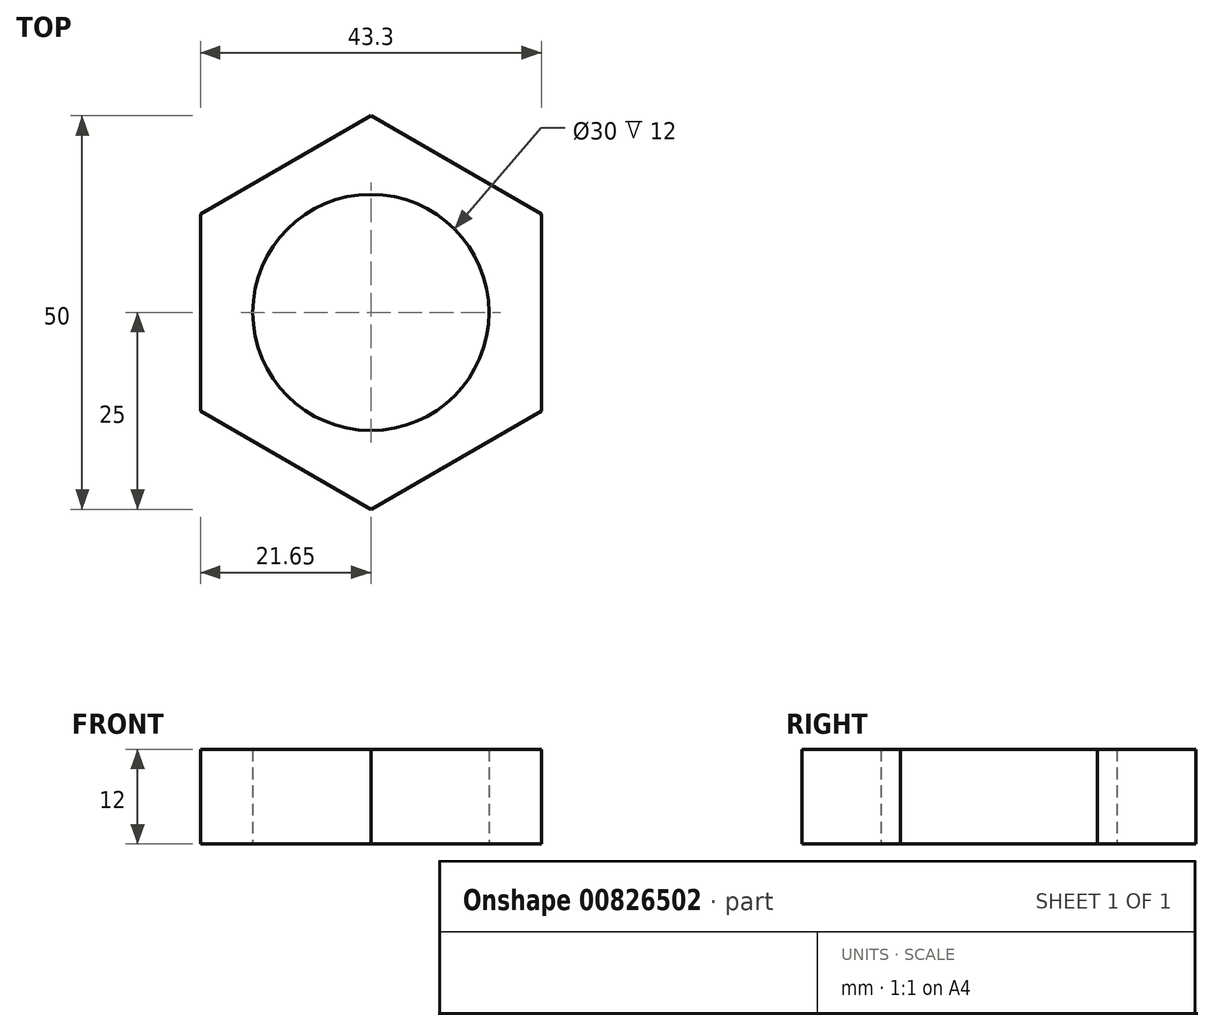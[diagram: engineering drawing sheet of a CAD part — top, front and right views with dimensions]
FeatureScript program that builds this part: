
annotation { "Feature Type Name" : "Feature", "Feature Type Description" : "" }
export const myFeature = defineFeature(function(context is Context, id is Id, definition is map)
    precondition{}
    {
        {
            var Q0;
            Q0=qCreatedBy(makeId("Top.planeOp"),FACE);
            var sketch = newSketch(context, id + "F0", { "sketchPlane" : qUnion([Q0])});
            skCircle(sketch, "E0", {"center": v(0, 0) * mm, "radius": 15 * mm});
            skLineSegment(sketch, "E1.0", {"start": v(0, 25) * mm, "end": v(21.65, 12.5) * mm});
            skLineSegment(sketch, "E1.1", {"start": v(21.65, 12.5) * mm, "end": v(21.65, -12.5) * mm});
            skLineSegment(sketch, "E1.2", {"start": v(21.65, -12.5) * mm, "end": v(0, -25) * mm});
            skLineSegment(sketch, "E1.3", {"start": v(0, -25) * mm, "end": v(-21.65, -12.5) * mm});
            skLineSegment(sketch, "E1.4", {"start": v(-21.65, -12.5) * mm, "end": v(-21.65, 12.5) * mm});
            skLineSegment(sketch, "E1.5", {"start": v(-21.65, 12.5) * mm, "end": v(0, 25) * mm});
            skSolve(sketch);
        }
        {
            var Q0;
            Q0 = qSketchRegion(id + "F0", true);
            extrude(context, id + "F1", {"entities" : qUnion([Q0]), "depth" : 12 * mm, "offsetDistance" : 25 * mm});
        }
    });
